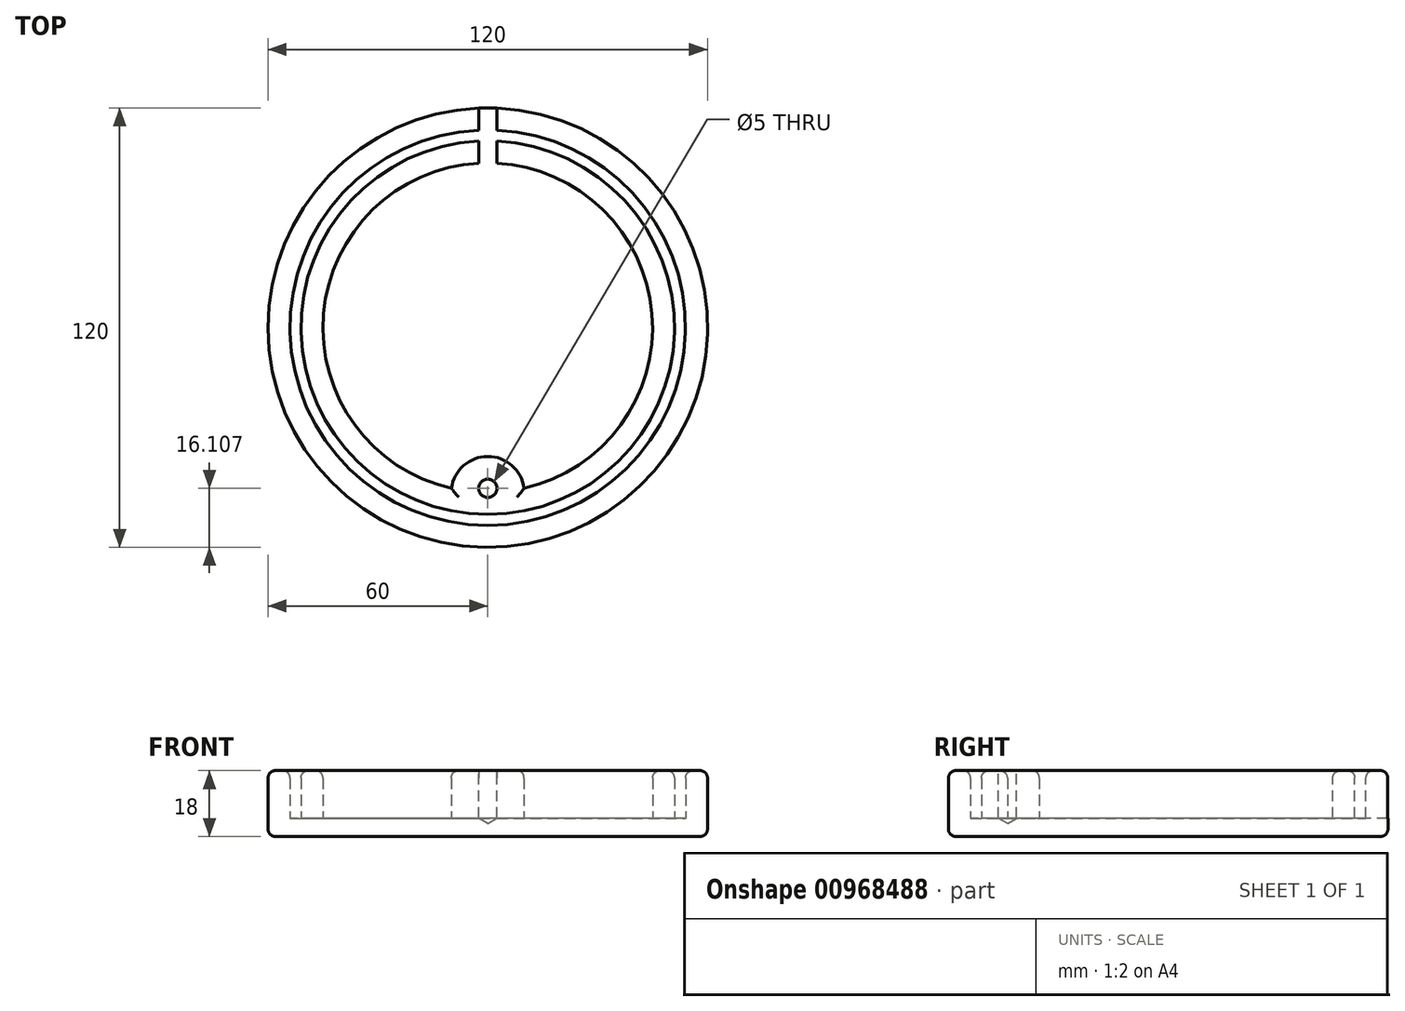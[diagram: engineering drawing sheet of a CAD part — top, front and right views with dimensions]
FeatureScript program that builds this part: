
annotation { "Feature Type Name" : "Feature", "Feature Type Description" : "" }
export const myFeature = defineFeature(function(context is Context, id is Id, definition is map)
    precondition{}
    {
        {
            var Q0;
            Q0=qCreatedBy(makeId("Front.planeOp"),FACE);
            var sketch = newSketch(context, id + "F0", { "sketchPlane" : qUnion([Q0])});
            skLineSegment(sketch, "E0.bottom", {"start": v(0, 0) * mm, "end": v(60, 0) * mm});
            skLineSegment(sketch, "E0.top", {"start": v(0, 5) * mm, "end": v(60, 5) * mm});
            skLineSegment(sketch, "E0.left", {"start": v(0, 0) * mm, "end": v(0, 5) * mm});
            skLineSegment(sketch, "E0.right", {"start": v(60, 0) * mm, "end": v(60, 5) * mm});
            skLineSegment(sketch, "E1.bottom", {"start": v(60, 5) * mm, "end": v(54, 5) * mm});
            skLineSegment(sketch, "E1.top", {"start": v(60, 18) * mm, "end": v(54, 18) * mm});
            skLineSegment(sketch, "E1.left", {"start": v(60, 5) * mm, "end": v(60, 18) * mm});
            skLineSegment(sketch, "E1.right", {"start": v(54, 5) * mm, "end": v(54, 18) * mm});
            skLineSegment(sketch, "E2.bottom", {"start": v(51, 5) * mm, "end": v(45, 5) * mm});
            skLineSegment(sketch, "E2.top", {"start": v(51, 18) * mm, "end": v(45, 18) * mm});
            skLineSegment(sketch, "E2.left", {"start": v(51, 5) * mm, "end": v(51, 18) * mm});
            skLineSegment(sketch, "E2.right", {"start": v(45, 5) * mm, "end": v(45, 18) * mm});
            skLineSegment(sketch, "E3", {"start": v(0, 0) * mm, "end": v(0, 13.27) * mm});
            skLineSegment(sketch, "E4", {"start": v(0, 0) * mm, "end": v(0, -26.73) * mm});
            skSolve(sketch);
        }
        {
            var Q0;
            Q0=makeQuery(id+"F0.imprint","IMPRINT",FACE,{"disambiguationData":[TD([[makeQuery(id+"F0.imprint","IMPRINT",EDGE,{"derivedFrom":sQuery(id+"F0.wireOp",EDGE,"E0.bottom")}),1.0]])]});
            var Q1;
            {var subQ2=sQuery(id+"F0.wireOp",EDGE,"E2.right");Q1=makeQuery(id+"F0.imprint","IMPRINT",FACE,{"disambiguationData":[TD([[makeQuery(id+"F0.imprint","IMPRINT",EDGE,{"derivedFrom":subQ2}),1.0]])]});}
            var Q2;
            Q2=makeQuery(id+"F0.imprint","IMPRINT",FACE,{"disambiguationData":[TD([[makeQuery(id+"F0.imprint","IMPRINT",EDGE,{"derivedFrom":sQuery(id+"F0.wireOp",EDGE,"E2.top")}),1.0]])]});
            var Q3;
            Q3=makeQuery(id+"F0.imprint","IMPRINT",FACE,{"disambiguationData":[TD([[makeQuery(id+"F0.imprint","IMPRINT",EDGE,{"derivedFrom":sQuery(id+"F0.wireOp",EDGE,"E1.top")}),1.0]])]});
            var Q4;
            Q4=sQuery(id+"F0.wireOp",EDGE,"E3");
            revolve(context, id + "F1", {"surfaceOperationType" : NewSurfaceOperationType.NEW, "entities" : qUnion([Q0, Q1, Q2, Q3]), "axis" : qUnion([Q4]), "revolveType" : RevolveType.FULL});
        }
        {
            var Q0;
            Q0=makeQuery(id+"F1.opRevolve","SWEPT_FACE",FACE,{"disambiguationData":[OSD([sQuery(id+"F0.wireOp",EDGE,"E2.top")])]});
            var sketch = newSketch(context, id + "F2", { "sketchPlane" : qUnion([Q0])});
            skLineSegment(sketch, "E5", {"start": v(0, 45) * mm, "end": v(0, 51) * mm});
            skLineSegment(sketch, "E6", {"start": v(0, 51) * mm, "end": v(2.5, 51) * mm});
            skLineSegment(sketch, "E7.MirrorCS", {"start": v(0, 51) * mm, "end": v(-2.5, 51) * mm});
            skLineSegment(sketch, "E8", {"start": v(2.5, 51) * mm, "end": v(2.5, 30.76) * mm});
            skPoint(sketch, "E9", {"position": v(2.5, 50.94) * mm});
            skPoint(sketch, "E9.positionSnap0", {"position": v(2.5, 40.88) * mm});
            skPoint(sketch, "E10.MirrorP", {"position": v(-2.5, 50.94) * mm});
            skLineSegment(sketch, "E11", {"start": v(-2.5, 50.94) * mm, "end": v(-2.5, 44.93) * mm});
            skLineSegment(sketch, "E12", {"start": v(2.5, 50.94) * mm, "end": v(2.5, 44.93) * mm});
            skSolve(sketch);
        }
        {
            var Q0;
            {var subQ0=sQuery(id+"F2.wireOp",EDGE,"E5");Q0=makeQuery(id+"F2.imprint","IMPRINT",FACE,{"disambiguationData":[TD([[makeQuery(id+"F2.imprint","IMPRINT",EDGE,{"derivedFrom":subQ0}),1.0]])]});}
            var Q1;
            {var subQ0=sQuery(id+"F2.wireOp",EDGE,"E5");Q1=makeQuery(id+"F2.imprint","IMPRINT",FACE,{"disambiguationData":[TD([[makeQuery(id+"F2.imprint","IMPRINT",EDGE,{"derivedFrom":subQ0}),-1.0]])]});}
            extrude(context, id + "F3", {"entities" : qUnion([Q0, Q1]), "operationType" : NewBodyOperationType.REMOVE, "oppositeDirection" : true, "depth" : 13 * mm, "offsetDistance" : 25 * mm});
        }
        {
            var Q0;
            Q0=makeQuery(id+"F1.opRevolve","SWEPT_EDGE",EDGE,{"disambiguationData":[OSD([sQuery(id+"F0.wireOp",EDGE,"E0.bottom"),sQuery(id+"F0.wireOp",EDGE,"E0.right")])]});
            fillet(context, id + "F4", {"entities" : qUnion([Q0]), "radius" : 2 * mm, "tangentPropagation" : true, "allowEdgeOverflow" : false});
        }
        {
            var Q0;
            Q0=makeQuery(id+"F1.opRevolve","SWEPT_FACE",FACE,{"disambiguationData":[OSD([sQuery(id+"F0.wireOp",EDGE,"E1.top")])]});
            var sketch = newSketch(context, id + "F5", { "sketchPlane" : qUnion([Q0])});
            skLineSegment(sketch, "E13", {"start": v(0, 60) * mm, "end": v(0, 54) * mm});
            skLineSegment(sketch, "E14", {"start": v(0, 60) * mm, "end": v(2.5, 60) * mm});
            skLineSegment(sketch, "E15.MirrorCS", {"start": v(0, 60) * mm, "end": v(-2.5, 60) * mm});
            skLineSegment(sketch, "E16", {"start": v(-2.5, 60) * mm, "end": v(-3.98, 59.87) * mm});
            skLineSegment(sketch, "E17", {"start": v(2.5, 60) * mm, "end": v(3.98, 59.87) * mm});
            skLineSegment(sketch, "E18", {"start": v(-3.98, 59.87) * mm, "end": v(-3.98, 53.85) * mm});
            skLineSegment(sketch, "E19", {"start": v(3.98, 59.87) * mm, "end": v(3.98, 53.85) * mm});
            skLineSegment(sketch, "E20", {"start": v(-2.5, 60) * mm, "end": v(-2.5, 53.94) * mm});
            skLineSegment(sketch, "E21", {"start": v(2.5, 60) * mm, "end": v(2.5, 53.94) * mm});
            skSolve(sketch);
        }
        {
            var Q0;
            {var subQ0=sQuery(id+"F0.wireOp",EDGE,"E2.right");var subQ1=sQuery(id+"F0.wireOp",EDGE,"E2.left");var subQ2=sQuery(id+"F0.wireOp",EDGE,"E0.top");Q0=makeQuery(id+"F3.boolean.opBoolean","MERGE",FACE,{"derivedFrom":[makeQuery(id+"F1.opRevolve","SWEPT_FACE",FACE,{"disambiguationData":[OSD([subQ2]),TDD([makeQuery(id+"F0.imprint","IMPRINT",EDGE,{"disambiguationData":[TD([[makeQuery(id+"F0.imprint","INTERSECT",VERTEX,{"derivedFrom":[subQ2,sQuery(id+"F0.wireOp",EDGE,"E0.left")]}),-1.0]])],"derivedFrom":subQ2})])]}),makeQuery(id+"F1.opRevolve","SWEPT_FACE",FACE,{"disambiguationData":[OSD([subQ2]),TDD([makeQuery(id+"F0.imprint","IMPRINT",EDGE,{"disambiguationData":[TD([[makeQuery(id+"F0.imprint","INTERSECT",VERTEX,{"derivedFrom":[subQ2,sQuery(id+"F0.wireOp",EDGE,"E1.right")]}),1.0]])],"derivedFrom":subQ2})])]})],"fromTools":[makeQuery(id+"F3.opExtrude","CAP_FACE",FACE,{"disambiguationData":[OSD([sQuery(id+"F0.wireOp",EDGE,"E2.top"),subQ1,subQ0,sQuery(id+"F2.wireOp",EDGE,"E8"),sQuery(id+"F2.wireOp",EDGE,"E11")])],"isStart":false})]});}
            var sketch = newSketch(context, id + "F6", { "sketchPlane" : qUnion([Q0])});
            skLineSegment(sketch, "E22", {"start": v(0, -45) * mm, "end": v(0, -25.36) * mm});
            skLineSegment(sketch, "E23", {"start": v(0, -35.18) * mm, "end": v(28.06, -35.18) * mm});
            skLineSegment(sketch, "E24.MirrorCS", {"start": v(0, -35.18) * mm, "end": v(-28.06, -35.18) * mm});
            skLineSegment(sketch, "E25", {"start": v(0, -45) * mm, "end": v(10, -45) * mm});
            skLineSegment(sketch, "E26.MirrorCS", {"start": v(0, -45) * mm, "end": v(-10, -45) * mm});
            skArc(sketch, "E27", {"start": v(10, -45) * mm, "mid": v(0, -35.18) * mm, "end": v(-10, -45) * mm});
            skPoint(sketch, "E28", {"position": v(0, -40.18) * mm});
            skSolve(sketch);
        }
        {
            var Q0;
            {var subQ0=sQuery(id+"F6.wireOp",EDGE,"E22");var subQ3=sQuery(id+"F6.wireOp",EDGE,"E27");var subQ4=makeQuery(id+"F6.imprint","INTERSECT",VERTEX,{"derivedFrom":[subQ0,sQuery(id+"F6.wireOp",EDGE,"E23"),sQuery(id+"F6.wireOp",EDGE,"E24.MirrorCS"),subQ3]});Q0=makeQuery(id+"F6.imprint","IMPRINT",FACE,{"disambiguationData":[TD([[makeQuery(id+"F6.imprint","IMPRINT",EDGE,{"disambiguationData":[TD([[subQ4,1.0]])],"derivedFrom":subQ3}),1.0]])]});}
            var Q1;
            {var subQ0=sQuery(id+"F6.wireOp",EDGE,"E22");var subQ3=sQuery(id+"F6.wireOp",EDGE,"E27");var subQ4=makeQuery(id+"F6.imprint","INTERSECT",VERTEX,{"derivedFrom":[subQ0,sQuery(id+"F6.wireOp",EDGE,"E23"),sQuery(id+"F6.wireOp",EDGE,"E24.MirrorCS"),subQ3]});Q1=makeQuery(id+"F6.imprint","IMPRINT",FACE,{"disambiguationData":[TD([[makeQuery(id+"F6.imprint","IMPRINT",EDGE,{"disambiguationData":[TD([[subQ4,-1.0]])],"derivedFrom":subQ3}),1.0]])]});}
            extrude(context, id + "F7", {"entities" : qUnion([Q0, Q1]), "operationType" : NewBodyOperationType.ADD, "depth" : 13 * mm, "offsetDistance" : 25 * mm});
        }
        {
            var Q0;
            Q0=makeQuery(id+"F7.boolean.opBoolean","MERGE",FACE,{"derivedFrom":[makeQuery(id+"F1.opRevolve","SWEPT_FACE",FACE,{"disambiguationData":[OSD([sQuery(id+"F0.wireOp",EDGE,"E2.top")])]}),makeQuery(id+"F7.opExtrude","CAP_FACE",FACE,{"disambiguationData":[OSD([sQuery(id+"F0.wireOp",EDGE,"E0.top"),sQuery(id+"F0.wireOp",EDGE,"E2.right"),sQuery(id+"F6.wireOp",EDGE,"E27")])],"isStart":false})]});
            var sketch = newSketch(context, id + "F8", { "sketchPlane" : qUnion([Q0])});
            skPoint(sketch, "E29", {"position": v(0, -35.18) * mm});
            skPoint(sketch, "E30", {"position": v(0, -43.9) * mm});
            skSolve(sketch);
        }
        {
            var Q0;
            Q0=sQuery(id+"F8.wireOp",VERTEX,"E30");
            var Q1;
            Q1=makeQuery(id+"F1.opRevolve","SWEPT_BODY",BODY,{"disambiguationData":[OSD([sQuery(id+"F0.wireOp",EDGE,"E0.bottom"),sQuery(id+"F0.wireOp",EDGE,"E0.top"),sQuery(id+"F0.wireOp",EDGE,"E0.left"),sQuery(id+"F0.wireOp",EDGE,"E0.right"),sQuery(id+"F0.wireOp",EDGE,"E1.top"),sQuery(id+"F0.wireOp",EDGE,"E1.left"),sQuery(id+"F0.wireOp",EDGE,"E1.right"),sQuery(id+"F0.wireOp",EDGE,"E2.top"),sQuery(id+"F0.wireOp",EDGE,"E2.left"),sQuery(id+"F0.wireOp",EDGE,"E2.right")])]});
            hole(context, id + "F9", {"style" : HoleStyle.SIMPLE, "endStyle" : HoleEndStyle.BLIND, "holeDiameter" : 5 * mm, "majorDiameter" : 5 * mm, "holeDepth" : 13 * mm, "isTappedThrough" : true, "tappedDepth" : 12 * mm, "tapClearance" : 3, "locations" : qUnion([Q0]), "scope" : qUnion([Q1])});
        }
        {
            var Q0;
            Q0=makeQuery(id+"F1.opRevolve","SWEPT_EDGE",EDGE,{"disambiguationData":[OSD([sQuery(id+"F0.wireOp",EDGE,"E1.top"),sQuery(id+"F0.wireOp",EDGE,"E1.left")])]});
            var Q1;
            Q1=makeQuery(id+"F1.opRevolve","SWEPT_EDGE",EDGE,{"disambiguationData":[OSD([sQuery(id+"F0.wireOp",EDGE,"E1.top"),sQuery(id+"F0.wireOp",EDGE,"E1.right")])]});
            var Q2;
            Q2=makeQuery(id+"F1.opRevolve","SWEPT_EDGE",EDGE,{"disambiguationData":[OSD([sQuery(id+"F0.wireOp",EDGE,"E2.top"),sQuery(id+"F0.wireOp",EDGE,"E2.left")])]});
            var Q3;
            {var subQ1=sQuery(id+"F0.wireOp",EDGE,"E2.right");var subQ2=sQuery(id+"F0.wireOp",EDGE,"E2.top");Q3=makeQuery(id+"F7.boolean.opBoolean","SPLIT",EDGE,{"disambiguationData":[TD([makeQuery(id+"F3.boolean.opBoolean","COPY",FACE,{"derivedFrom":makeQuery(id+"F3.opExtrude","SWEPT_FACE",FACE,{"disambiguationData":[OSD([sQuery(id+"F2.wireOp",EDGE,"E11")])]})})])],"derivedFrom":makeQuery(id+"F1.opRevolve","SWEPT_EDGE",EDGE,{"disambiguationData":[OSD([subQ2,subQ1])]})});}
            var Q4;
            {var subQ1=sQuery(id+"F0.wireOp",EDGE,"E2.top");var subQ2=sQuery(id+"F0.wireOp",EDGE,"E2.right");Q4=makeQuery(id+"F7.boolean.opBoolean","SPLIT",EDGE,{"disambiguationData":[TD([makeQuery(id+"F3.boolean.opBoolean","COPY",FACE,{"derivedFrom":makeQuery(id+"F3.opExtrude","SWEPT_FACE",FACE,{"disambiguationData":[OSD([sQuery(id+"F2.wireOp",EDGE,"E8")])]})})])],"derivedFrom":makeQuery(id+"F1.opRevolve","SWEPT_EDGE",EDGE,{"disambiguationData":[OSD([subQ1,subQ2])]})});}
            var Q5;
            Q5=makeQuery(id+"F7.opExtrude","CAP_EDGE",EDGE,{"disambiguationData":[OSD([sQuery(id+"F6.wireOp",EDGE,"E27")])],"isStart":false});
            fillet(context, id + "F10", {"entities" : qUnion([Q0, Q1, Q2, Q3, Q4, Q5]), "radius" : 2 * mm, "tangentPropagation" : true, "allowEdgeOverflow" : false});
        }
        {
            var Q0;
            {var subQ0=sQuery(id+"F5.wireOp",EDGE,"E13");Q0=makeQuery(id+"F5.imprint","IMPRINT",FACE,{"disambiguationData":[TD([[makeQuery(id+"F5.imprint","IMPRINT",EDGE,{"derivedFrom":subQ0}),1.0]])]});}
            var Q1;
            {var subQ0=sQuery(id+"F5.wireOp",EDGE,"E13");Q1=makeQuery(id+"F5.imprint","IMPRINT",FACE,{"disambiguationData":[TD([[makeQuery(id+"F5.imprint","IMPRINT",EDGE,{"derivedFrom":subQ0}),-1.0]])]});}
            extrude(context, id + "F11", {"entities" : qUnion([Q0, Q1]), "operationType" : NewBodyOperationType.REMOVE, "oppositeDirection" : true, "depth" : 13 * mm, "offsetDistance" : 25 * mm});
        }
    });
